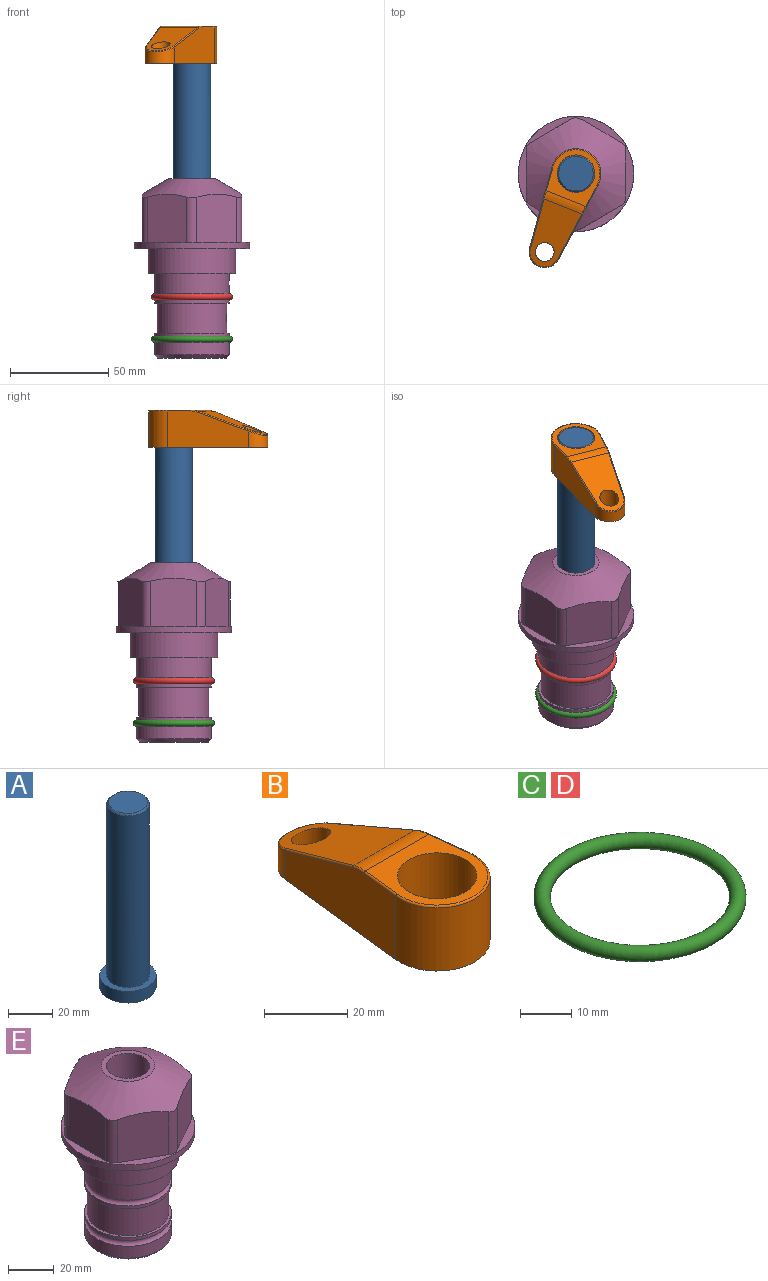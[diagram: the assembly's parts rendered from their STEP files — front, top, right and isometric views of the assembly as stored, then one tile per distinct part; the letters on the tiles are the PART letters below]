
ASSEMBLY  parts=5 mates=3
PART A: 6 faces, bbox 25.4x25.4x101.6 mm
  f0: plane 17.46x17.46mm, normal (0,0,1), area 239.5mm2, adj f5
  f1: plane 25.4x25.4mm, normal (0,0,-1), area 506.7mm2, adj f2
  f2: cylinder r=12.7mm len=25.4mm, axis (0,0,1), area 506.7mm2, adj f1,f3
  f3: plane 25.4x25.4mm, normal (0,0,1), area 221.7mm2, adj f2,f4
  f4: cylinder r=9.53mm len=94.46mm, axis (0,0,1), area 5653mm2, adj f3,f5
  f5: cone r=8.73mm half-angle=45deg, axis (0,0,-1), area 64.4mm2, adj f0,f4
PART B: 44 faces, bbox 27.5x64.5x19.1 mm
  f0: plane 2.3x0.95mm, normal (0,0,-1), area 1mm2, adj f25,f30,f34
  f1: plane 63.5x25.4mm, normal (0,0,-1), area 561.7mm2, adj f2,f3,f4,f5,f6,f7,f19,f20
  f2: cylinder r=12.7mm len=25.4mm, axis (0,0,-1), area 792.2mm2, adj f1,f3,f5,f13
  f3: plane 42.33x18.54mm, normal (0.99,0.11,0), area 647mm2, adj f1,f2,f4,f11,f12,f14
  f4: cylinder r=7.94mm len=15.78mm, axis (0,0,-1), area 158.6mm2, adj f1,f3,f5,f16
  f5: plane 42.33x18.54mm, normal (-0.99,0.11,0), area 647mm2, adj f1,f2,f4,f15,f17,f18
  f6: cylinder r=9.53mm len=19.05mm, axis (0,0,-1), area 1140.1mm2, adj f1,f8
  f7: cylinder r=4.76mm len=10.98mm, axis (0,0,-1), area 276.1mm2, adj f1,f9
  f8: plane 25.83x24.38mm, normal (0,0,1), area 262.2mm2, adj f6,f10,f11,f13,f15
  f9: plane 32.49x20.55mm, normal (0,0.34,0.94), area 489.9mm2, adj f7,f10,f14,f16,f18
  f10: cylinder r=12.7mm len=21.49mm, axis (-1,0,0), area 93.2mm2, adj f8,f9,f12,f17
  f11: cylinder r=0.51mm len=12.34mm, axis (0.11,-0.99,0), area 9.9mm2, adj f3,f8,f12,f13
  f12: bspline ~7.62x1.64mm, area 3.5mm2, adj f3,f10,f11,f14
  f13: torus R=12.19mm, axis (0,0,1), area 33.6mm2, adj f2,f8,f11,f15
  f14: cylinder r=0.51mm len=26.01mm, axis (0.1,-0.93,0.34), area 21.6mm2, adj f3,f9,f12,f16
  f15: cylinder r=0.51mm len=12.34mm, axis (0.11,0.99,0), area 9.9mm2, adj f5,f8,f13,f17
  f16: bspline ~15.78x7.05mm, area 15.7mm2, adj f4,f9,f14,f18
  f17: bspline ~7.62x1.64mm, area 3.5mm2, adj f5,f10,f15,f18
  f18: cylinder r=0.51mm len=26.01mm, axis (0.1,0.93,-0.34), area 21.6mm2, adj f5,f9,f16,f17
  f19: plane 21.6x14.29mm, normal (-0.99,-0.11,0), area 242.6mm2, adj f1,f26,f28,f34,f36,f38
  f20: plane 21.6x14.29mm, normal (0.99,-0.11,0), area 242.6mm2, adj f1,f27,f29,f37,f39,f41
  f21: cylinder r=12.7mm len=14.29mm, axis (0,0,-1), area 173.2mm2, adj f1,f26,f27,f30,f31,f33
  f22: cylinder r=7.94mm len=7.63mm, axis (0,0,-1), area 53.8mm2, adj f1,f28,f29,f42
  f23: plane 2.3x0.95mm, normal (0,0,-1), area 1mm2, adj f25,f33,f37
  f24: plane 17.94x12.32mm, normal (0,-0.34,-0.94), area 191.2mm2, adj f25,f38,f41,f42
  f25: cylinder r=9.53mm len=12.93mm, axis (-1,0,0), area 37.5mm2, adj f0,f23,f24,f31,f36,f39
  f26: cylinder r=1.59mm len=14.29mm, axis (0,0,-1), area 49mm2, adj f1,f19,f21,f32
  f27: cylinder r=1.59mm len=14.29mm, axis (0,0,-1), area 49mm2, adj f1,f20,f21,f35
  f28: cylinder r=1.59mm len=7.28mm, axis (0,0,-1), area 22.1mm2, adj f1,f19,f22,f40
  f29: cylinder r=1.59mm len=7.28mm, axis (0,0,-1), area 22.1mm2, adj f1,f20,f22,f43
  f30: torus R=14.29mm, axis (0,0,1), area 5.8mm2, adj f0,f21,f31,f32
  f31: bspline ~11.06x2.73mm, area 20.8mm2, adj f21,f25,f30,f33
  f32: sphere r=1.59mm, area 5.4mm2, adj f26,f30,f34
  f33: torus R=14.29mm, axis (0,0,1), area 5.8mm2, adj f21,f23,f31,f35
  f34: cylinder r=1.59mm len=1.68mm, axis (-0.11,0.99,0), area 2.4mm2, adj f0,f19,f32,f36
  f35: sphere r=1.59mm, area 5.4mm2, adj f27,f33,f37
  f36: bspline ~5.82x2.33mm, area 7.7mm2, adj f19,f25,f34,f38
  f37: cylinder r=1.59mm len=1.68mm, axis (0.11,0.99,0), area 2.4mm2, adj f20,f23,f35,f39
  f38: cylinder r=1.59mm len=18.33mm, axis (0.1,-0.93,0.34), area 46.7mm2, adj f19,f24,f36,f40
  f39: bspline ~5.82x2.33mm, area 7.7mm2, adj f20,f25,f37,f41
  f40: sphere r=1.59mm, area 3.6mm2, adj f28,f38,f42
  f41: cylinder r=1.59mm len=18.33mm, axis (0.1,0.93,-0.34), area 46.7mm2, adj f20,f24,f39,f43
  f42: bspline ~8.31x1.84mm, area 15.3mm2, adj f22,f24,f40,f43
  f43: sphere r=1.59mm, area 3.6mm2, adj f29,f41,f42
PART C: 1 faces, bbox 44.7x44.7x3.2 mm
  f0: torus R=19.05mm, axis (0,0,1), area 1193.9mm2
PART D: same geometry as C
PART E: 36 faces, bbox 58.7x58.7x91.2 mm
  f0: cylinder r=17.78mm len=35.56mm, axis (0,0,1), area 1670.8mm2, adj f23,f24,f31
  f1: cylinder r=19.05mm len=38.1mm, axis (0,0,1), area 1191.9mm2, adj f26,f27,f30
  f2: plane 58.66x58.66mm, normal (0,0,-1), area 1150.6mm2, adj f3,f28
  f3: cylinder r=29.33mm len=58.66mm, axis (0,0,-1), area 585.1mm2, adj f2,f4
  f4: plane 58.66x58.66mm, normal (0,0,1), area 475.9mm2, adj f3,f5,f6,f7,f8,f9,f10,f11
  f5: plane 24.5x20.32mm, normal (-0.5,0.87,0), area 562.8mm2, adj f4,f15,f16,f17
  f6: plane 24.5x20.32mm, normal (0.5,0.87,0), area 562.8mm2, adj f4,f14,f15,f17
  f7: plane 24.5x23.48mm, normal (1,0,0), area 562.8mm2, adj f4,f13,f14,f17
  f8: plane 24.5x20.32mm, normal (0.5,-0.87,0), area 562.8mm2, adj f4,f12,f13,f17
  f9: plane 24.5x20.32mm, normal (-0.5,-0.87,0), area 562.8mm2, adj f4,f11,f12,f17
  f10: plane 24.5x23.48mm, normal (-1,0,0), area 562.8mm2, adj f4,f11,f16,f17
  f11: cylinder r=5.08mm len=23.01mm, axis (0,0,-1), area 121.2mm2, adj f4,f9,f10,f17
  f12: cylinder r=5.08mm len=23.01mm, axis (0,0,-1), area 121.2mm2, adj f4,f8,f9,f17
  f13: cylinder r=5.08mm len=23.01mm, axis (0,0,-1), area 121.2mm2, adj f4,f7,f8,f17
  f14: cylinder r=5.08mm len=23.01mm, axis (0,0,-1), area 121.2mm2, adj f4,f6,f7,f17
  f15: cylinder r=5.08mm len=23.01mm, axis (0,0,-1), area 121.2mm2, adj f4,f5,f6,f17
  f16: cylinder r=5.08mm len=23.01mm, axis (0,0,-1), area 121.2mm2, adj f4,f5,f10,f17
  f17: cone r=11.73mm half-angle=60deg, axis (0,0,-1), area 2071.8mm2, adj f5,f6,f7,f8,f9,f10,f11,f12
  f18: plane 23.46x23.46mm, normal (0,0,1), area 147.4mm2, adj f17,f35
  f19: plane 34.93x34.93mm, normal (0,0,-1), area 958mm2, adj f29
  f20: cylinder r=19.05mm len=38.1mm, axis (0,0,1), area 760.1mm2, adj f21,f29
  f21: torus R=19.05mm, axis (0,0,1), area 565.3mm2, adj f20,f22
  f22: cylinder r=19.05mm len=38.1mm, axis (0,0,1), area 190mm2, adj f21,f23
  f23: plane 38.1x38.1mm, normal (0,0,1), area 146.9mm2, adj f0,f22
  f24: plane 38.1x38.1mm, normal (0,0,-1), area 146.9mm2, adj f0,f25
  f25: cylinder r=19.05mm len=38.1mm, axis (0,0,1), area 190mm2, adj f24,f26
  f26: torus R=19.05mm, axis (0,0,1), area 565.3mm2, adj f1,f25
  f27: plane 44.45x44.45mm, normal (0,0,-1), area 411.7mm2, adj f1,f28
  f28: cylinder r=22.23mm len=44.45mm, axis (0,0,1), area 1773.5mm2, adj f2,f27
  f29: cone r=19.05mm half-angle=45deg, axis (0,0,1), area 257.5mm2, adj f19,f20
  f30: cylinder r=3.17mm len=6.75mm, axis (-1,0,0), area 128mm2, adj f1,f33
  f31: cylinder r=3.17mm len=6.35mm, axis (-1,0,0), area 102.5mm2, adj f0,f33
  f32: plane 25.4x25.4mm, normal (0,0,1), area 506.7mm2, adj f33
  f33: cylinder r=12.7mm len=66.42mm, axis (0,0,-1), area 5236.2mm2, adj f30,f31,f32,f34
  f34: cone r=9.53mm half-angle=30deg, axis (0,0,-1), area 443.4mm2, adj f33,f35
  f35: cylinder r=9.53mm len=19.05mm, axis (0,0,-1), area 849mm2, adj f18,f34
PLACE A rot(axis=(0,0,-1),111.8deg) t=(0,0,39.53)mm
PLACE B rot(axis=(0,0,1),158.2deg) t=(0,0,94.14)mm
PLACE C t=(0,0,-21.59)mm
PLACE D at identity
PLACE E at identity fixed
MATE fastened C.f0 <-> E.f0  axis (0,0,1) through (0,0,-46.1)mm
MATE cylindrical A.f2 <-> E.f0  axis (0,0,1) through (0,0,65.17)mm
MATE fastened B.f2 <-> A.f2  axis (0,0,1) through (0,0,113.19)mm
